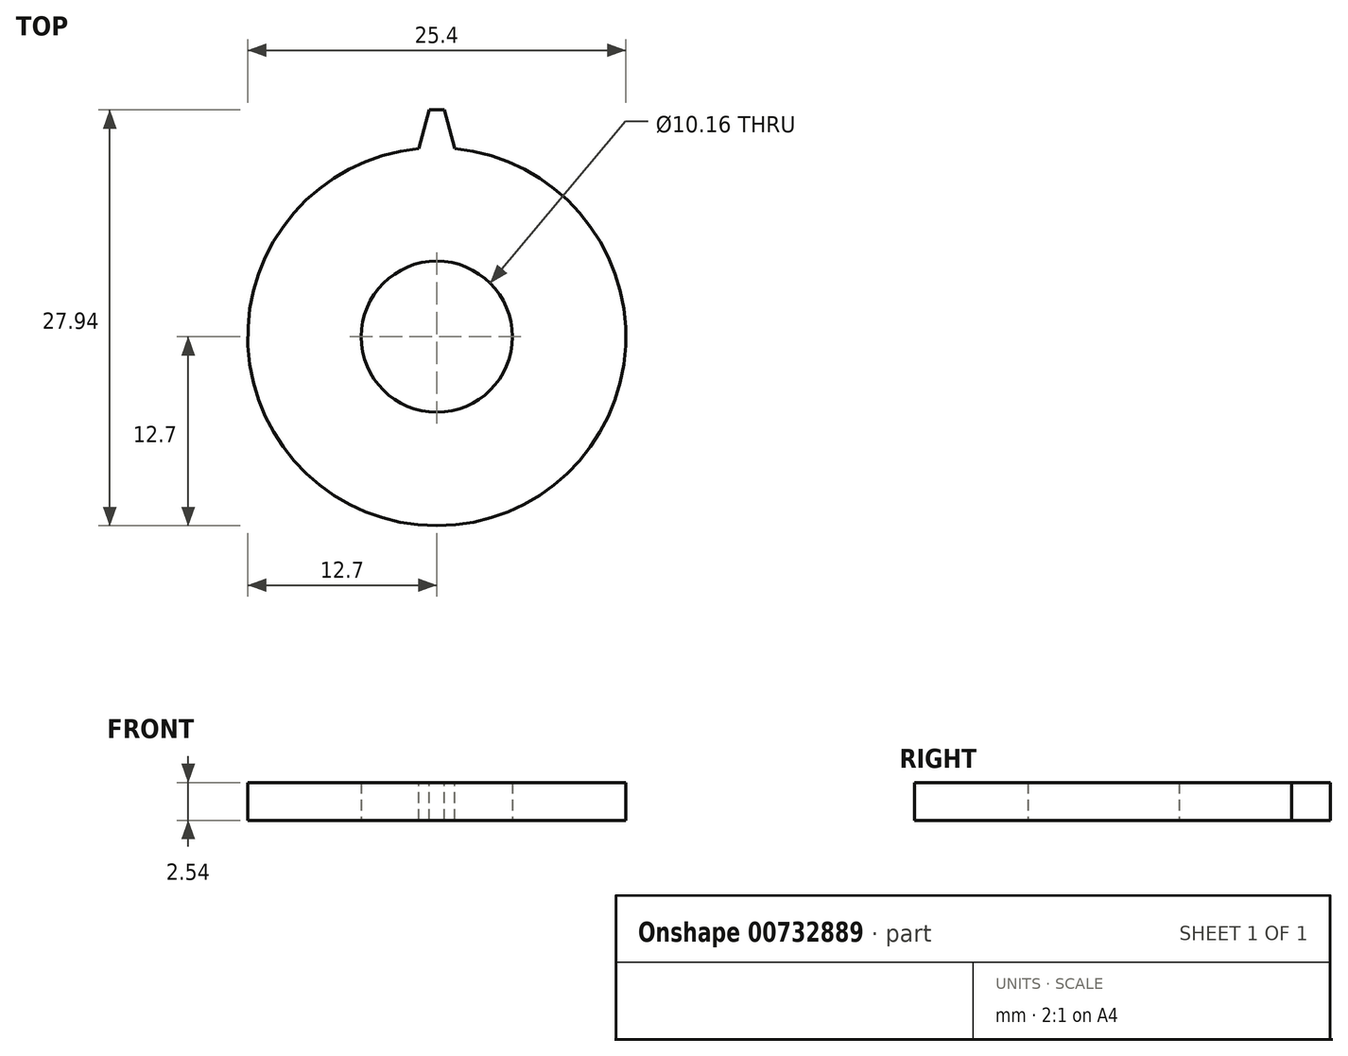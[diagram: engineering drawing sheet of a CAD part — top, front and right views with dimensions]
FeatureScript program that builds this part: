
annotation { "Feature Type Name" : "Feature", "Feature Type Description" : "" }
export const myFeature = defineFeature(function(context is Context, id is Id, definition is map)
    precondition{}
    {
        {
            var Q0;
            Q0=qCreatedBy(makeId("Top.planeOp"),FACE);
            var sketch = newSketch(context, id + "F0", { "sketchPlane" : qUnion([Q0])});
            skCircle(sketch, "E0", {"center": v(0, 0) * mm, "radius": 12.7 * mm});
            skCircle(sketch, "E1", {"center": v(0, 0) * mm, "radius": 5.08 * mm});
            skSolve(sketch);
        }
        {
            var Q0;
            Q0 = qSketchRegion(id + "F0", true);
            extrude(context, id + "F1", {"entities" : qUnion([Q0]), "depth" : 2.54 * mm, "offsetDistance" : 25.4 * mm});
        }
        {
            var Q0;
            Q0=makeQuery(id+"F1.opExtrude","CAP_FACE",FACE,{"disambiguationData":[OSD([sQuery(id+"F0.wireOp",EDGE,"E0")])],"isStart":false});
            var sketch = newSketch(context, id + "F2", { "sketchPlane" : qUnion([Q0])});
            skLineSegment(sketch, "E2", {"start": v(0, 0) * mm, "end": v(0, 15.24) * mm, "construction": true});
            skLineSegment(sketch, "E3", {"start": v(1.32, 12.2) * mm, "end": v(0.5, 15.24) * mm});
            skLineSegment(sketch, "E4", {"start": v(0.5, 15.24) * mm, "end": v(0, 15.24) * mm});
            skLineSegment(sketch, "E5", {"start": v(-0.5, 15.24) * mm, "end": v(-1.32, 12.2) * mm});
            skLineSegment(sketch, "E6", {"start": v(-0.5, 15.24) * mm, "end": v(0, 15.24) * mm});
            skSolve(sketch);
        }
        {
            var Q0;
            {var subQ0=sQuery(id+"F2.wireOp",EDGE,"B36icRHa-D8fN-QKRy-Czzo-95UYKd0kPyGu");Q0=makeQuery(id+"F2.imprint","IMPRINT",FACE,{"disambiguationData":[TD([[makeQuery(id+"F2.imprint","IMPRINT",EDGE,{"derivedFrom":subQ0}),1.0]])]});}
            var Q1;
            {var subQ4=sQuery(id+"F2.wireOp",EDGE,"E4");Q1=makeQuery(id+"F2.imprint","IMPRINT",FACE,{"disambiguationData":[TD([[makeQuery(id+"F2.imprint","IMPRINT",EDGE,{"derivedFrom":subQ4}),1.0]])]});}
            extrude(context, id + "F3", {"entities" : qUnion([Q0, Q1]), "operationType" : NewBodyOperationType.ADD, "oppositeDirection" : true, "depth" : 2.54 * mm, "offsetDistance" : 25.4 * mm});
        }
    });
